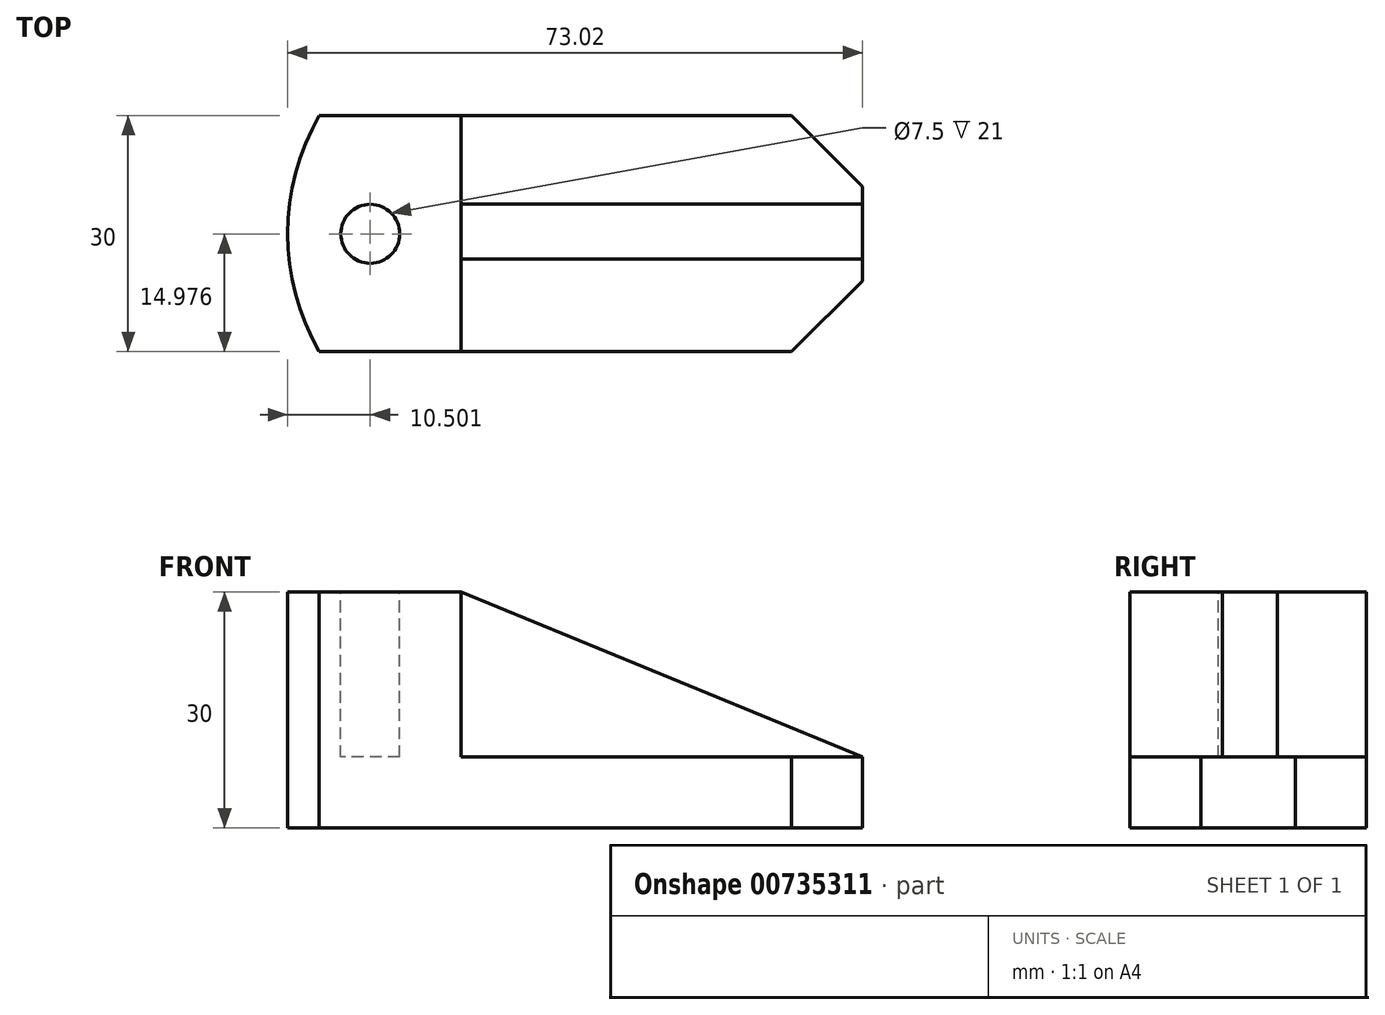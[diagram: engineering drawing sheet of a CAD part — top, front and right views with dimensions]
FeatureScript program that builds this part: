
annotation { "Feature Type Name" : "Feature", "Feature Type Description" : "" }
export const myFeature = defineFeature(function(context is Context, id is Id, definition is map)
    precondition{}
    {
        {
            var Q0;
            Q0=qCreatedBy(makeId("Top.planeOp"),FACE);
            var sketch = newSketch(context, id + "F0", { "sketchPlane" : qUnion([Q0])});
            skLineSegment(sketch, "E0", {"start": v(0, -30) * mm, "end": v(60, -30) * mm});
            skLineSegment(sketch, "E1", {"start": v(60, -30) * mm, "end": v(69, -21) * mm});
            skLineSegment(sketch, "E2", {"start": v(69, -21) * mm, "end": v(69, -9) * mm});
            skLineSegment(sketch, "E3", {"start": v(69, -9) * mm, "end": v(60, 0) * mm});
            skLineSegment(sketch, "E4", {"start": v(60, 0) * mm, "end": v(0, 0) * mm});
            skArc(sketch, "E5", {"start": v(0, 0) * mm, "mid": v(-4.02, -15) * mm, "end": v(0, -30) * mm});
            skSolve(sketch);
        }
        {
            var Q0;
            Q0 = qSketchRegion(id + "F0", true);
            extrude(context, id + "F1", {"entities" : qUnion([Q0]), "depth" : 9 * mm, "offsetDistance" : 25 * mm});
        }
        {
            var Q0;
            Q0=makeQuery(id+"F1.opExtrude","CAP_FACE",FACE,{"disambiguationData":[OSD([sQuery(id+"F0.wireOp",EDGE,"E0"),sQuery(id+"F0.wireOp",EDGE,"E1"),sQuery(id+"F0.wireOp",EDGE,"E2"),sQuery(id+"F0.wireOp",EDGE,"E3"),sQuery(id+"F0.wireOp",EDGE,"E4"),sQuery(id+"F0.wireOp",EDGE,"E5")])],"isStart":false});
            var sketch = newSketch(context, id + "F2", { "sketchPlane" : qUnion([Q0])});
            skLineSegment(sketch, "E6", {"start": v(18, -30) * mm, "end": v(18, 0) * mm});
            skSolve(sketch);
        }
        {
            var Q0;
            Q0 = qSketchRegion(id + "F2", true);
            var Q1;
            {var subQ0=sQuery(id+"F2.wireOp",EDGE,"E6");Q1=makeQuery(id+"F2.imprint","IMPRINT",FACE,{"disambiguationData":[TD([[makeQuery(id+"F2.imprint","IMPRINT",EDGE,{"derivedFrom":subQ0}),1.0]])]});}
            extrude(context, id + "F3", {"entities" : qUnion([Q0, Q1]), "operationType" : NewBodyOperationType.ADD, "depth" : 21 * mm, "offsetDistance" : 25 * mm});
        }
        {
            var Q0;
            Q0=makeQuery(id+"F1.opExtrude","CAP_FACE",FACE,{"disambiguationData":[OSD([sQuery(id+"F0.wireOp",EDGE,"E0"),sQuery(id+"F0.wireOp",EDGE,"E1"),sQuery(id+"F0.wireOp",EDGE,"E2"),sQuery(id+"F0.wireOp",EDGE,"E3"),sQuery(id+"F0.wireOp",EDGE,"E4"),sQuery(id+"F0.wireOp",EDGE,"E5")])],"isStart":false});
            var sketch = newSketch(context, id + "F4", { "sketchPlane" : qUnion([Q0])});
            skPoint(sketch, "E7.end.orphan", {"position": v(69, -15) * mm});
            skPoint(sketch, "E8.end.orphan", {"position": v(18, -15) * mm});
            skLineSegment(sketch, "E9", {"start": v(69, -18.25) * mm, "end": v(18, -18.25) * mm});
            skLineSegment(sketch, "E10", {"start": v(18, -18.25) * mm, "end": v(18, -11.25) * mm});
            skLineSegment(sketch, "E11", {"start": v(18, -11.25) * mm, "end": v(69, -11.25) * mm});
            skLineSegment(sketch, "E12", {"start": v(69, -11.25) * mm, "end": v(69, -18.25) * mm});
            skSolve(sketch);
        }
        {
            var Q0;
            Q0 = qSketchRegion(id + "F4", true);
            extrude(context, id + "F5", {"entities" : qUnion([Q0]), "operationType" : NewBodyOperationType.ADD, "depth" : 21 * mm, "offsetDistance" : 25 * mm});
        }
        {
            var Q0;
            Q0=makeQuery(id+"F5.opExtrude","SWEPT_FACE",FACE,{"disambiguationData":[OSD([sQuery(id+"F4.wireOp",EDGE,"E9")])]});
            var sketch = newSketch(context, id + "F6", { "sketchPlane" : qUnion([Q0])});
            skLineSegment(sketch, "E13", {"start": v(18, 30) * mm, "end": v(69, 9) * mm});
            skLineSegment(sketch, "E14", {"start": v(69, 9) * mm, "end": v(69, 30) * mm});
            skLineSegment(sketch, "E15", {"start": v(69, 30) * mm, "end": v(18, 30) * mm});
            skSolve(sketch);
        }
        {
            var Q0;
            Q0=makeQuery(id+"F6.imprint","IMPRINT",FACE,{"disambiguationData":[TD([[makeQuery(id+"F6.imprint","IMPRINT",EDGE,{"derivedFrom":sQuery(id+"F6.wireOp",EDGE,"E13")}),1.0]])]});
            extrude(context, id + "F7", {"entities" : qUnion([Q0]), "operationType" : NewBodyOperationType.REMOVE, "oppositeDirection" : true, "depth" : 25 * mm, "offsetDistance" : 25 * mm});
        }
        {
            var Q0;
            Q0=makeQuery(id+"F5.boolean.opBoolean","MERGE",FACE,{"derivedFrom":[makeQuery(id+"F3.opExtrude","CAP_FACE",FACE,{"disambiguationData":[OSD([sQuery(id+"F0.wireOp",EDGE,"E0"),sQuery(id+"F0.wireOp",EDGE,"E4"),sQuery(id+"F0.wireOp",EDGE,"E5"),sQuery(id+"F2.wireOp",EDGE,"E6")])],"isStart":false}),makeQuery(id+"F5.opExtrude","CAP_FACE",FACE,{"disambiguationData":[OSD([sQuery(id+"F4.wireOp",EDGE,"E9"),sQuery(id+"F4.wireOp",EDGE,"E10"),sQuery(id+"F4.wireOp",EDGE,"E11"),sQuery(id+"F4.wireOp",EDGE,"E12")])],"isStart":false})]});
            var sketch = newSketch(context, id + "F8", { "sketchPlane" : qUnion([Q0])});
            skCircle(sketch, "E16", {"center": v(6.48, -15.02) * mm, "radius": 3.75 * mm});
            skSolve(sketch);
        }
        {
            var Q0;
            Q0=makeQuery(id+"F8.imprint","IMPRINT",FACE,{"disambiguationData":[TD([[makeQuery(id+"F8.imprint","IMPRINT",EDGE,{"derivedFrom":sQuery(id+"F8.wireOp",EDGE,"E16")}),1.0]])]});
            extrude(context, id + "F9", {"entities" : qUnion([Q0]), "operationType" : NewBodyOperationType.REMOVE, "oppositeDirection" : true, "depth" : 21 * mm, "offsetDistance" : 25 * mm});
        }
    });
